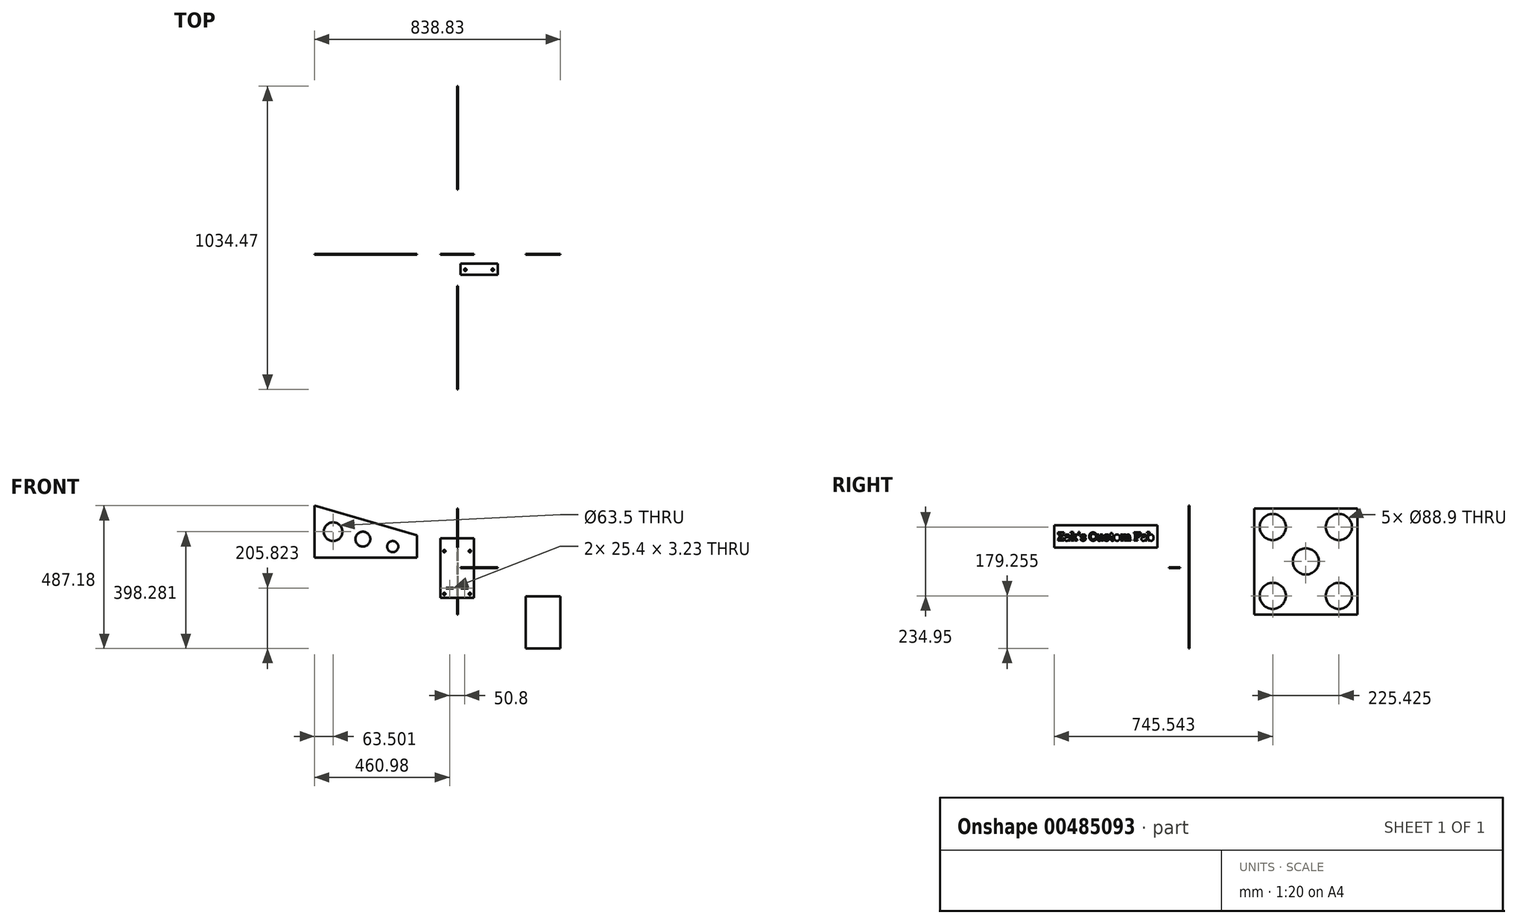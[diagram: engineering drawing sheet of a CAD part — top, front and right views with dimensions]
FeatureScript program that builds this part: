
annotation { "Feature Type Name" : "Feature", "Feature Type Description" : "" }
export const myFeature = defineFeature(function(context is Context, id is Id, definition is map)
    precondition{}
    {
        {
            var Q0;
            Q0=qCreatedBy(makeId("Front.planeOp"),FACE);
            var sketch = newSketch(context, id + "F0", { "sketchPlane" : qUnion([Q0])});
            skLineSegment(sketch, "E0.bottom", {"start": v(-57.15, 101.6) * mm, "end": v(57.15, 101.6) * mm});
            skLineSegment(sketch, "E0.top", {"start": v(-57.15, -101.6) * mm, "end": v(57.15, -101.6) * mm});
            skLineSegment(sketch, "E0.left", {"start": v(-57.15, 101.6) * mm, "end": v(-57.15, -101.6) * mm});
            skLineSegment(sketch, "E0.right", {"start": v(57.15, 101.6) * mm, "end": v(57.15, -101.6) * mm});
            skPoint(sketch, "E0.middle", {"position": v(0, 0) * mm});
            skCircle(sketch, "E1", {"center": v(43.66, 57.94) * mm, "radius": 3.97 * mm});
            skCircle(sketch, "E2", {"center": v(-43.66, 57.94) * mm, "radius": 3.97 * mm});
            skCircle(sketch, "E3", {"center": v(43.66, -88.1) * mm, "radius": 3.97 * mm});
            skCircle(sketch, "E4", {"center": v(-43.66, -88.1) * mm, "radius": 3.97 * mm});
            skLineSegment(sketch, "E5.bottom", {"start": v(38.1, -66.62) * mm, "end": v(12.7, -66.62) * mm});
            skLineSegment(sketch, "E5.top", {"start": v(38.1, -69.85) * mm, "end": v(12.7, -69.85) * mm});
            skLineSegment(sketch, "E5.left", {"start": v(38.1, -66.62) * mm, "end": v(38.1, -69.85) * mm});
            skLineSegment(sketch, "E5.right", {"start": v(12.7, -66.62) * mm, "end": v(12.7, -69.85) * mm});
            skLineSegment(sketch, "E6.bottom", {"start": v(-12.7, -66.62) * mm, "end": v(-38.1, -66.62) * mm});
            skLineSegment(sketch, "E6.top", {"start": v(-12.7, -69.85) * mm, "end": v(-38.1, -69.85) * mm});
            skLineSegment(sketch, "E6.left", {"start": v(-12.7, -66.62) * mm, "end": v(-12.7, -69.85) * mm});
            skLineSegment(sketch, "E6.right", {"start": v(-38.1, -66.62) * mm, "end": v(-38.1, -69.85) * mm});
            skSolve(sketch);
        }
        {
            var Q0;
            Q0=makeQuery(id+"F0.imprint","IMPRINT",FACE,{"disambiguationData":[TD([[makeQuery(id+"F0.imprint","IMPRINT",EDGE,{"derivedFrom":sQuery(id+"F0.wireOp",EDGE,"E0.bottom")}),-1.0]])]});
            extrude(context, id + "F1", {"entities" : qUnion([Q0]), "depth" : 3.17 * mm});
        }
        {
            var Q0;
            Q0=qCreatedBy(makeId("Top.planeOp"),FACE);
            var sketch = newSketch(context, id + "F2", { "sketchPlane" : qUnion([Q0])});
            skLineSegment(sketch, "E7.bottom", {"start": v(138.07, -70.69) * mm, "end": v(11.07, -70.69) * mm});
            skLineSegment(sketch, "E7.top", {"start": v(138.07, -32.59) * mm, "end": v(11.07, -32.59) * mm});
            skLineSegment(sketch, "E7.left", {"start": v(138.07, -70.69) * mm, "end": v(138.07, -32.59) * mm});
            skLineSegment(sketch, "E7.right", {"start": v(11.07, -70.69) * mm, "end": v(11.07, -32.59) * mm});
            skCircle(sketch, "E8", {"center": v(121.4, -54.02) * mm, "radius": 3.97 * mm});
            skCircle(sketch, "E9", {"center": v(27.74, -54.02) * mm, "radius": 3.97 * mm});
            skSolve(sketch);
        }
        {
            var Q0;
            Q0=makeQuery(id+"F2.imprint","IMPRINT",FACE,{"disambiguationData":[TD([[makeQuery(id+"F2.imprint","IMPRINT",EDGE,{"derivedFrom":sQuery(id+"F2.wireOp",EDGE,"E7.bottom")}),-1.0]])]});
            extrude(context, id + "F3", {"entities" : qUnion([Q0]), "depth" : 3.17 * mm});
        }
        {
            var Q0;
            Q0=qCreatedBy(makeId("Right.planeOp"),FACE);
            var sketch = newSketch(context, id + "F4", { "sketchPlane" : qUnion([Q0])});
            skLineSegment(sketch, "E10.bottom", {"start": v(220.11, 203.64) * mm, "end": v(572.54, 203.64) * mm});
            skLineSegment(sketch, "E10.top", {"start": v(220.11, -158.3) * mm, "end": v(572.54, -158.3) * mm});
            skLineSegment(sketch, "E10.left", {"start": v(220.11, 203.64) * mm, "end": v(220.11, -158.3) * mm});
            skLineSegment(sketch, "E10.right", {"start": v(572.54, 203.64) * mm, "end": v(572.54, -158.3) * mm});
            skLineSegment(sketch, "E11.bottom", {"start": v(359.5, 203.64) * mm, "end": v(383.64, 203.64) * mm});
            skLineSegment(sketch, "E11.top", {"start": v(359.5, 206.82) * mm, "end": v(383.64, 206.82) * mm});
            skLineSegment(sketch, "E11.left", {"start": v(359.5, 203.64) * mm, "end": v(359.5, 206.82) * mm});
            skLineSegment(sketch, "E11.right", {"start": v(383.64, 203.64) * mm, "end": v(383.64, 206.82) * mm});
            skLineSegment(sketch, "E12.bottom", {"start": v(409.04, 203.64) * mm, "end": v(433.17, 203.64) * mm});
            skLineSegment(sketch, "E12.top", {"start": v(409.04, 206.82) * mm, "end": v(433.17, 206.82) * mm});
            skLineSegment(sketch, "E12.left", {"start": v(409.04, 203.64) * mm, "end": v(409.04, 206.82) * mm});
            skLineSegment(sketch, "E12.right", {"start": v(433.17, 203.64) * mm, "end": v(433.17, 206.82) * mm});
            skCircle(sketch, "E13", {"center": v(283.61, 140.14) * mm, "radius": 44.45 * mm});
            skCircle(sketch, "E14", {"center": v(509.04, 140.14) * mm, "radius": 44.45 * mm});
            skCircle(sketch, "E15", {"center": v(283.61, -94.8) * mm, "radius": 44.45 * mm});
            skCircle(sketch, "E16", {"center": v(509.04, -94.8) * mm, "radius": 44.45 * mm});
            skCircle(sketch, "E17", {"center": v(396.32, 22.67) * mm, "radius": 44.45 * mm});
            skPoint(sketch, "E17.centerSnap0", {"position": v(220.11, 22.67) * mm});
            skPoint(sketch, "E17.centerSnap1", {"position": v(396.32, -158.3) * mm});
            skSolve(sketch);
        }
        {
            var Q0;
            Q0=makeQuery(id+"F4.imprint","IMPRINT",FACE,{"disambiguationData":[TD([[makeQuery(id+"F4.imprint","IMPRINT",EDGE,{"derivedFrom":sQuery(id+"F4.wireOp",EDGE,"E10.top")}),1.0]])]});
            var Q1;
            Q1=makeQuery(id+"F4.imprint","IMPRINT",FACE,{"disambiguationData":[TD([[makeQuery(id+"F4.imprint","IMPRINT",EDGE,{"derivedFrom":sQuery(id+"F4.wireOp",EDGE,"E11.bottom")}),1.0]])]});
            var Q2;
            Q2=makeQuery(id+"F4.imprint","IMPRINT",FACE,{"disambiguationData":[TD([[makeQuery(id+"F4.imprint","IMPRINT",EDGE,{"derivedFrom":sQuery(id+"F4.wireOp",EDGE,"E12.bottom")}),1.0]])]});
            extrude(context, id + "F5", {"entities" : qUnion([Q0, Q1, Q2]), "depth" : 3.17 * mm});
        }
        {
            var Q0;
            Q0=qCreatedBy(makeId("Right.planeOp"),FACE);
            var sketch = newSketch(context, id + "F6", { "sketchPlane" : qUnion([Q0])});
            skLineSegment(sketch, "E18.bottom", {"start": v(-109.5, 146.81) * mm, "end": v(-461.93, 146.81) * mm});
            skLineSegment(sketch, "E18.top", {"start": v(-109.5, 70.61) * mm, "end": v(-461.93, 70.61) * mm});
            skLineSegment(sketch, "E18.left", {"start": v(-109.5, 146.81) * mm, "end": v(-109.5, 70.61) * mm});
            skLineSegment(sketch, "E18.right", {"start": v(-461.93, 146.81) * mm, "end": v(-461.93, 70.61) * mm});
            skText(sketch, "E19", { "text": "Zak\'s Custom Fab", "fontName": "RobotoSlab-Bold.ttf"});
            const initialGuessF6  = {"E19": [-0.45088, 0.09357, 1, 0, 0.0283]};
            skSetInitialGuess(sketch, initialGuessF6);
            skSolve(sketch);
        }
        {
            var Q0;
            Q0=makeQuery(id+"F6.imprint","IMPRINT",FACE,{"disambiguationData":[TD([[makeQuery(id+"F6.imprint","IMPRINT",EDGE,{"derivedFrom":sQuery(id+"F6.wireOp",EDGE,"E18.bottom")}),1.0]])]});
            extrude(context, id + "F7", {"entities" : qUnion([Q0]), "depth" : 3.17 * mm});
        }
        {
            var Q0;
            Q0=qCreatedBy(makeId("Front.planeOp"),FACE);
            var sketch = newSketch(context, id + "F8", { "sketchPlane" : qUnion([Q0])});
            skLineSegment(sketch, "E20", {"start": v(-486.38, 213.12) * mm, "end": v(-486.38, 35.32) * mm});
            skLineSegment(sketch, "E21", {"start": v(-486.38, 35.32) * mm, "end": v(-137.13, 35.32) * mm});
            skLineSegment(sketch, "E22", {"start": v(-137.13, 111.52) * mm, "end": v(-137.13, 35.32) * mm});
            skLineSegment(sketch, "E23", {"start": v(-137.13, 111.52) * mm, "end": v(-486.38, 213.12) * mm});
            skCircle(sketch, "E24", {"center": v(-422.88, 124.22) * mm, "radius": 31.75 * mm});
            skPoint(sketch, "E24.centerSnap0", {"position": v(-486.38, 124.22) * mm});
            skCircle(sketch, "E25", {"center": v(-321.28, 98.82) * mm, "radius": 25.4 * mm});
            skCircle(sketch, "E26", {"center": v(-219.68, 73.42) * mm, "radius": 19.05 * mm});
            skSolve(sketch);
        }
        {
            var Q0;
            Q0=makeQuery(id+"F8.imprint","IMPRINT",FACE,{"disambiguationData":[TD([[makeQuery(id+"F8.imprint","IMPRINT",EDGE,{"derivedFrom":sQuery(id+"F8.wireOp",EDGE,"E20")}),1.0]])]});
            extrude(context, id + "F9", {"entities" : qUnion([Q0]), "depth" : 3.17 * mm});
        }
        {
            var Q0;
            Q0=qCreatedBy(makeId("Front.planeOp"),FACE);
            var sketch = newSketch(context, id + "F10", { "sketchPlane" : qUnion([Q0])});
            skLineSegment(sketch, "E27.bottom", {"start": v(352.45, -96.26) * mm, "end": v(233.39, -96.26) * mm});
            skLineSegment(sketch, "E27.top", {"start": v(352.45, -274.06) * mm, "end": v(233.39, -274.06) * mm});
            skLineSegment(sketch, "E27.left", {"start": v(352.45, -96.26) * mm, "end": v(352.45, -274.06) * mm});
            skLineSegment(sketch, "E27.right", {"start": v(233.39, -96.26) * mm, "end": v(233.39, -274.06) * mm});
            skSolve(sketch);
        }
        {
            var Q0;
            Q0=makeQuery(id+"F10.imprint","IMPRINT",FACE,{"disambiguationData":[TD([[makeQuery(id+"F10.imprint","IMPRINT",EDGE,{"derivedFrom":sQuery(id+"F10.wireOp",EDGE,"E27.bottom")}),1.0]])]});
            extrude(context, id + "F11", {"entities" : qUnion([Q0]), "depth" : 3.17 * mm});
        }
    });
